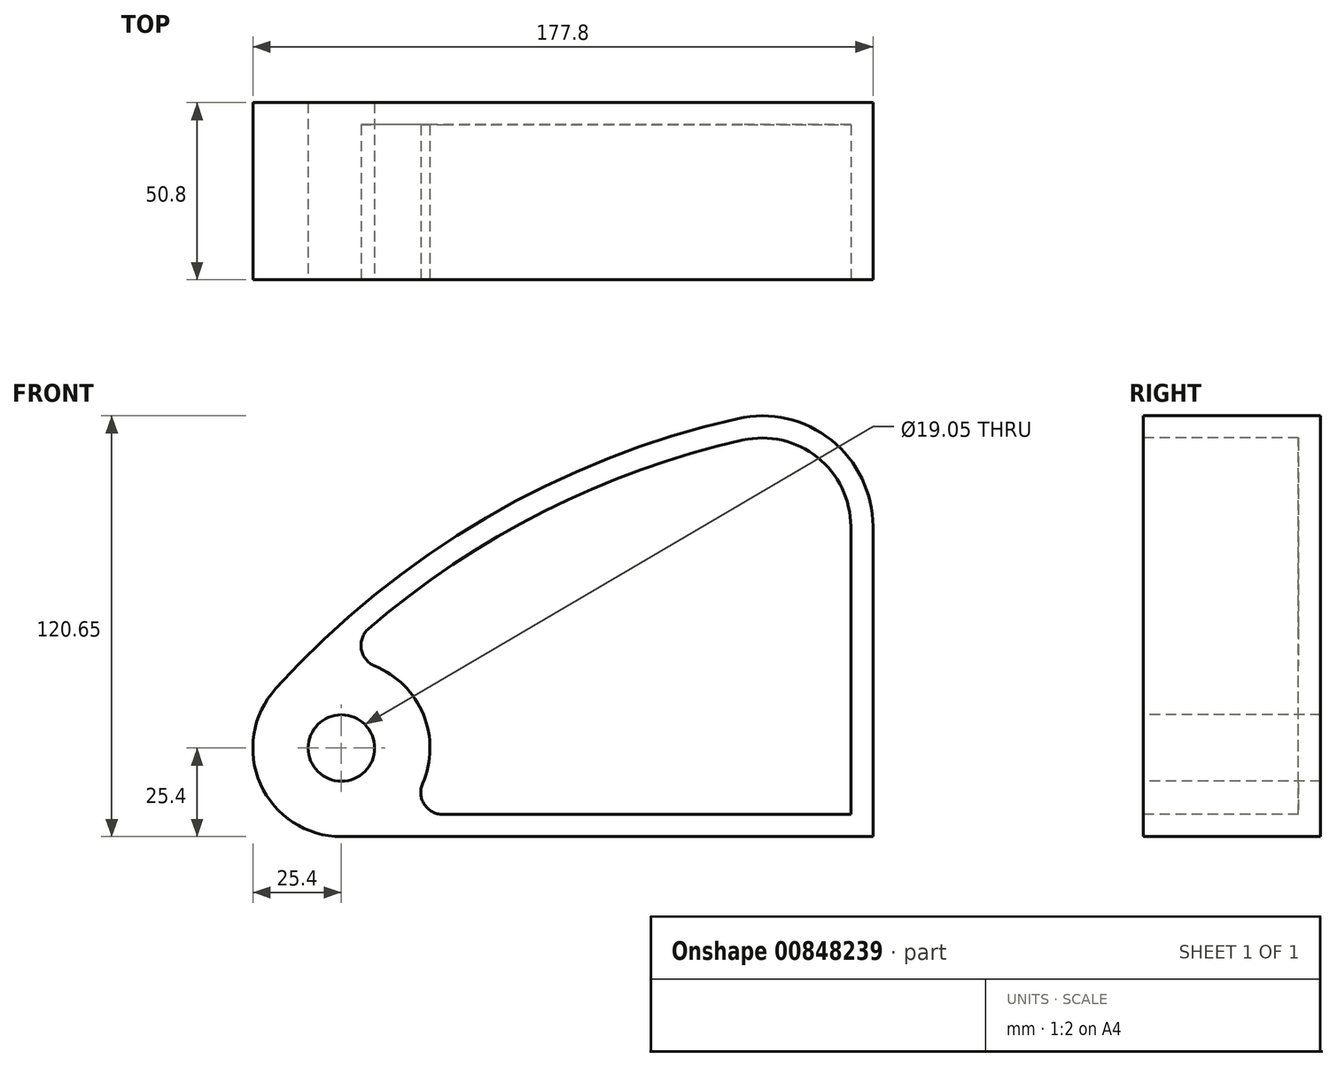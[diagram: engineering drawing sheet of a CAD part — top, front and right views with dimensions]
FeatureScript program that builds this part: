
annotation { "Feature Type Name" : "Feature", "Feature Type Description" : "" }
export const myFeature = defineFeature(function(context is Context, id is Id, definition is map)
    precondition{}
    {
        {
            var Q0;
            Q0=qCreatedBy(makeId("Front.planeOp"),FACE);
            var sketch = newSketch(context, id + "F0", { "sketchPlane" : qUnion([Q0])});
            skCircle(sketch, "E0", {"center": v(0, 0) * mm, "radius": 25.4 * mm});
            skCircle(sketch, "E1", {"center": v(120.65, 63.5) * mm, "radius": 31.75 * mm});
            skLineSegment(sketch, "E2", {"start": v(0, -25.4) * mm, "end": v(152.4, -25.4) * mm});
            skLineSegment(sketch, "E3", {"start": v(152.4, -25.4) * mm, "end": v(152.4, 63.5) * mm});
            skArc(sketch, "E4", {"start": v(113.66, 94.47) * mm, "mid": v(41.42, 66) * mm, "end": v(-18.84, 17.03) * mm});
            skSolve(sketch);
        }
        {
            var Q0;
            {var subQ1=sQuery(id+"F0.wireOp",EDGE,"E2");Q0=makeQuery(id+"F0.imprint","IMPRINT",FACE,{"disambiguationData":[TD([[makeQuery(id+"F0.imprint","IMPRINT",EDGE,{"derivedFrom":subQ1}),1.0]])]});}
            var Q1;
            {var subQ0=sQuery(id+"F0.wireOp",EDGE,"E1");var subQ1=makeQuery(id+"F0.imprint","INTERSECT",VERTEX,{"derivedFrom":[subQ0,sQuery(id+"F0.wireOp",EDGE,"E3")]});Q1=makeQuery(id+"F0.imprint","IMPRINT",FACE,{"disambiguationData":[TD([[makeQuery(id+"F0.imprint","IMPRINT",EDGE,{"disambiguationData":[TD([[subQ1,-1.0]])],"derivedFrom":subQ0}),1.0]])]});}
            var Q2;
            {var subQ0=sQuery(id+"F0.wireOp",EDGE,"E0");var subQ1=makeQuery(id+"F0.imprint","INTERSECT",VERTEX,{"derivedFrom":[subQ0,sQuery(id+"F0.wireOp",EDGE,"E2")]});Q2=makeQuery(id+"F0.imprint","IMPRINT",FACE,{"disambiguationData":[TD([[makeQuery(id+"F0.imprint","IMPRINT",EDGE,{"disambiguationData":[TD([[subQ1,1.0]])],"derivedFrom":subQ0}),1.0]])]});}
            extrude(context, id + "F1", {"entities" : qUnion([Q0, Q1, Q2]), "depth" : 50.8 * mm, "offsetDistance" : 25.4 * mm});
        }
        {
            var Q0;
            Q0=makeQuery(id+"F1.opExtrude","CAP_FACE",FACE,{"disambiguationData":[OSD([sQuery(id+"F0.wireOp",EDGE,"E0"),sQuery(id+"F0.wireOp",EDGE,"E1"),sQuery(id+"F0.wireOp",EDGE,"E2"),sQuery(id+"F0.wireOp",EDGE,"E3"),sQuery(id+"F0.wireOp",EDGE,"E4")])],"isStart":false});
            var sketch = newSketch(context, id + "F2", { "sketchPlane" : qUnion([Q0])});
            skCircle(sketch, "E5", {"center": v(0, 0) * mm, "radius": 25.4 * mm});
            skArc(sketch, "E6.0", {"start": v(146.05, 63.5) * mm, "mid": v(136.51, 83.34) * mm, "end": v(115.06, 88.28) * mm});
            skLineSegment(sketch, "E6.1", {"start": v(146.05, -19.05) * mm, "end": v(146.05, 63.5) * mm});
            skArc(sketch, "E6.2", {"start": v(115.06, 88.28) * mm, "mid": v(44.62, 60.52) * mm, "end": v(-14.13, 12.77) * mm});
            skArc(sketch, "E6.3", {"start": v(-14.13, 12.77) * mm, "mid": v(-17.41, -7.73) * mm, "end": v(0, -19.05) * mm});
            skLineSegment(sketch, "E6.4", {"start": v(0, -19.05) * mm, "end": v(146.05, -19.05) * mm});
            skSolve(sketch);
        }
        {
            var Q0;
            {var subQ1=sQuery(id+"F2.wireOp",EDGE,"E6.0");Q0=makeQuery(id+"F2.imprint","IMPRINT",FACE,{"disambiguationData":[TD([[makeQuery(id+"F2.imprint","IMPRINT",EDGE,{"derivedFrom":subQ1}),1.0]])]});}
            extrude(context, id + "F3", {"entities" : qUnion([Q0]), "operationType" : NewBodyOperationType.REMOVE, "oppositeDirection" : true, "depth" : 44.45 * mm, "offsetDistance" : 25.4 * mm});
        }
        {
            var Q0;
            Q0=makeQuery(id+"F1.opExtrude","CAP_FACE",FACE,{"disambiguationData":[OSD([sQuery(id+"F0.wireOp",EDGE,"E0"),sQuery(id+"F0.wireOp",EDGE,"E1"),sQuery(id+"F0.wireOp",EDGE,"E2"),sQuery(id+"F0.wireOp",EDGE,"E3"),sQuery(id+"F0.wireOp",EDGE,"E4")])],"isStart":false});
            var sketch = newSketch(context, id + "F4", { "sketchPlane" : qUnion([Q0])});
            skCircle(sketch, "E7", {"center": v(0, 0) * mm, "radius": 9.53 * mm});
            skSolve(sketch);
        }
        {
            var Q0;
            Q0=makeQuery(id+"F4.imprint","IMPRINT",FACE,{"disambiguationData":[TD([[makeQuery(id+"F4.imprint","IMPRINT",EDGE,{"derivedFrom":sQuery(id+"F4.wireOp",EDGE,"E7")}),1.0]])]});
            extrude(context, id + "F5", {"entities" : qUnion([Q0]), "operationType" : NewBodyOperationType.REMOVE, "endBound" : BoundingType.THROUGH_ALL, "oppositeDirection" : true, "depth" : 25.4 * mm, "offsetDistance" : 25.4 * mm});
        }
        {
            var Q0;
            Q0=makeQuery(id+"F3.boolean.opBoolean","COPY",EDGE,{"derivedFrom":makeQuery(id+"F3.opExtrude","SWEPT_EDGE",EDGE,{"disambiguationData":[OSD([sQuery(id+"F2.wireOp",EDGE,"E5"),sQuery(id+"F2.wireOp",EDGE,"E6.4")])]})});
            var Q1;
            Q1=makeQuery(id+"F3.boolean.opBoolean","COPY",EDGE,{"derivedFrom":makeQuery(id+"F3.opExtrude","SWEPT_EDGE",EDGE,{"disambiguationData":[OSD([sQuery(id+"F2.wireOp",EDGE,"E5"),sQuery(id+"F2.wireOp",EDGE,"E6.2")])]})});
            fillet(context, id + "F6", {"entities" : qUnion([Q0, Q1]), "radius" : 6.35 * mm, "tangentPropagation" : true, "allowEdgeOverflow" : false});
        }
    });
